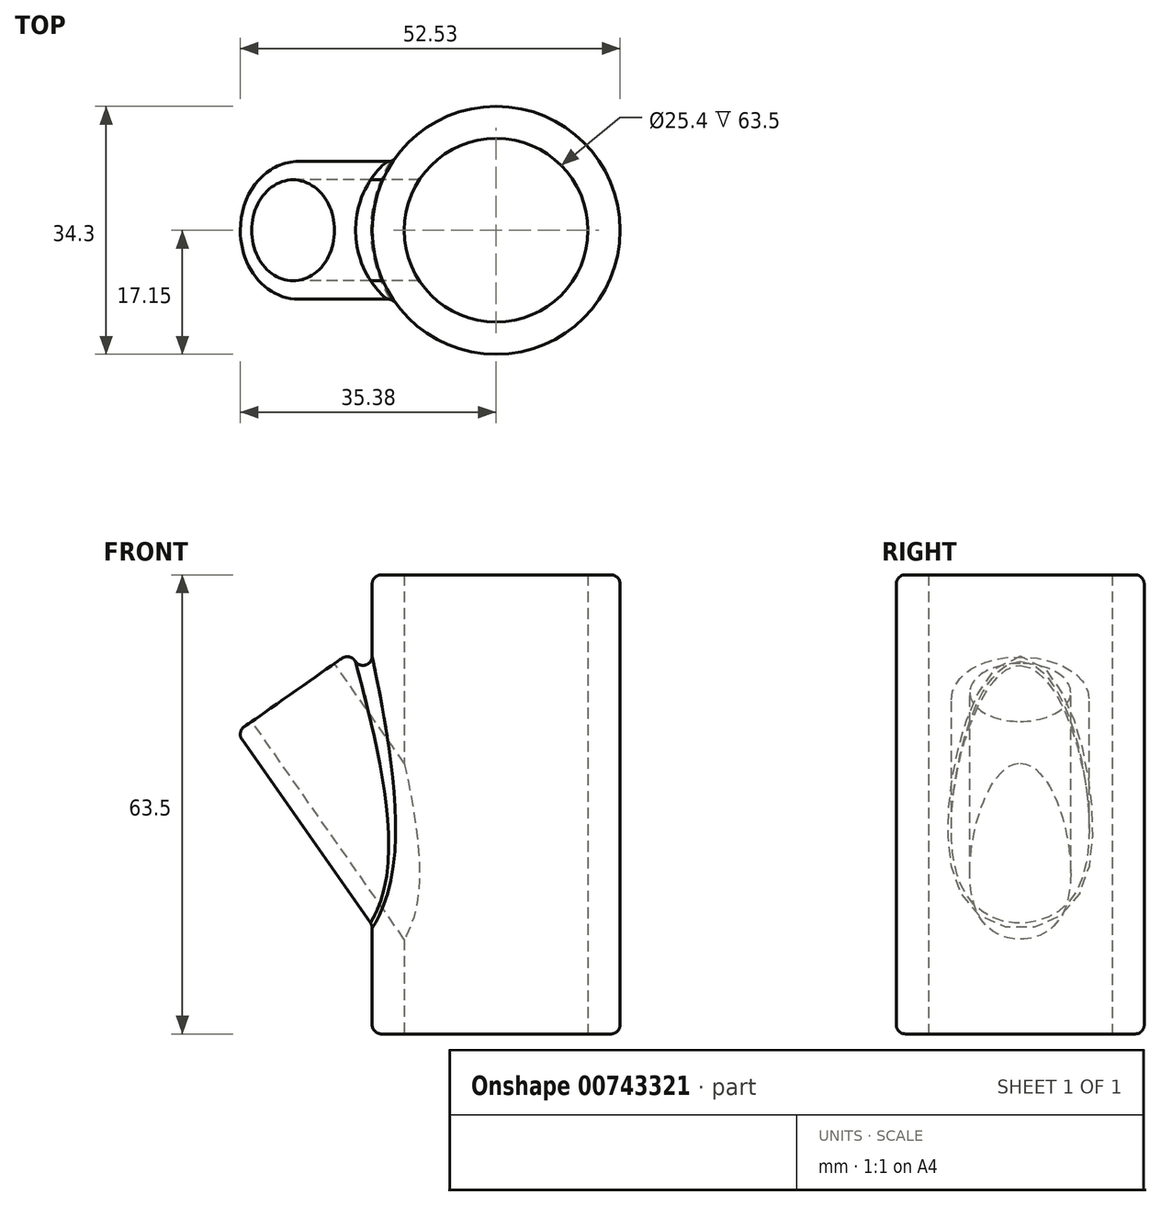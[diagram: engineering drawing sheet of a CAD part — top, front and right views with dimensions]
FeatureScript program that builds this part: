
annotation { "Feature Type Name" : "Feature", "Feature Type Description" : "" }
export const myFeature = defineFeature(function(context is Context, id is Id, definition is map)
    precondition{}
    {
        {
            var Q0;
            Q0=qCreatedBy(makeId("Top.planeOp"),FACE);
            var sketch = newSketch(context, id + "F0", { "sketchPlane" : qUnion([Q0])});
            skCircle(sketch, "E0", {"center": v(0, 0) * mm, "radius": 12.7 * mm});
            skCircle(sketch, "E1", {"center": v(0, 0) * mm, "radius": 17.15 * mm});
            skSolve(sketch);
        }
        {
            var Q0;
            Q0=makeQuery(id+"F0.imprint","IMPRINT",FACE,{"disambiguationData":[TD([[makeQuery(id+"F0.imprint","IMPRINT",EDGE,{"derivedFrom":sQuery(id+"F0.wireOp",EDGE,"E0")}),-1.0]])]});
            extrude(context, id + "F1", {"entities" : qUnion([Q0]), "depth" : 63.5 * mm, "offsetDistance" : 25.4 * mm});
        }
        {
            var Q0;
            Q0=qCreatedBy(makeId("Right.planeOp"),FACE);
            cPlane(context, id + "F2", {"entities" : qUnion([Q0]), "cplaneType" : CPlaneType.OFFSET, "offset" : 16.76 * mm, "oppositeDirection" : true, "width" : 152.4 * mm, "height" : 152.4 * mm});
        }
        {
            var Q0;
            Q0=qCreatedBy(id+"F2.planeOp",FACE);
            var sketch = newSketch(context, id + "F3", { "sketchPlane" : qUnion([Q0])});
            skLineSegment(sketch, "E2", {"start": v(45.22, 55.14) * mm, "end": v(-44.35, 55.14) * mm});
            skSolve(sketch);
        }
        {
            var Q0;
            Q0=sQuery(id+"F3.wireOp",EDGE,"E2");
            cPlane(context, id + "F4", {"entities" : qUnion([Q0]), "cplaneType" : CPlaneType.LINE_ANGLE, "offset" : 25.4 * mm, "angle" : 35 * degree, "width" : 152.4 * mm, "height" : 152.4 * mm});
        }
        {
            var Q0;
            Q0=qCreatedBy(id+"F4.planeOp",FACE);
            var sketch = newSketch(context, id + "F5", { "sketchPlane" : qUnion([Q0])});
            skCircle(sketch, "E3", {"center": v(4.09, 0) * mm, "radius": 6.99 * mm});
            skCircle(sketch, "E4", {"center": v(4.09, 0) * mm, "radius": 9.53 * mm});
            skSolve(sketch);
        }
        {
            var Q0;
            Q0=makeQuery(id+"F5.imprint","IMPRINT",FACE,{"disambiguationData":[TD([[makeQuery(id+"F5.imprint","IMPRINT",EDGE,{"derivedFrom":sQuery(id+"F5.wireOp",EDGE,"E3")}),-1.0]])]});
            extrude(context, id + "F6", {"entities" : qUnion([Q0]), "operationType" : NewBodyOperationType.ADD, "depth" : 35.56 * mm, "offsetDistance" : 25.4 * mm});
        }
        {
            var Q0;
            Q0=makeQuery(id+"F6.opExtrude","CAP_FACE",FACE,{"disambiguationData":[OSD([sQuery(id+"F5.wireOp",EDGE,"E3"),sQuery(id+"F5.wireOp",EDGE,"E4")])],"isStart":true});
            var sketch = newSketch(context, id + "F7", { "sketchPlane" : qUnion([Q0])});
            skCircle(sketch, "E5", {"center": v(4.09, 0) * mm, "radius": 6.99 * mm});
            skSolve(sketch);
        }
        {
            var Q0;
            Q0 = qSketchRegion(id + "F7", true);
            extrude(context, id + "F8", {"entities" : qUnion([Q0]), "operationType" : NewBodyOperationType.REMOVE, "oppositeDirection" : true, "depth" : 43.38 * mm, "offsetDistance" : 25.4 * mm});
        }
        {
            var Q0;
            {var subQ0=sQuery(id+"F5.wireOp",EDGE,"E4");Q0=makeQuery(id+"F6.boolean.opBoolean","SPLIT",FACE,{"disambiguationData":[TD([makeQuery(id+"F1.opExtrude","SWEPT_FACE",FACE,{"disambiguationData":[OSD([sQuery(id+"F0.wireOp",EDGE,"E1")])]})])],"derivedFrom":makeQuery(id+"F6.opExtrude","SWEPT_FACE",FACE,{"disambiguationData":[OSD([subQ0])]})});}
            var Q1;
            Q1=makeQuery(id+"F1.opExtrude","CAP_EDGE",EDGE,{"disambiguationData":[OSD([sQuery(id+"F0.wireOp",EDGE,"E1")])],"isStart":false});
            var Q2;
            Q2=makeQuery(id+"F1.opExtrude","CAP_EDGE",EDGE,{"disambiguationData":[OSD([sQuery(id+"F0.wireOp",EDGE,"E1")])],"isStart":true});
            fillet(context, id + "F9", {"entities" : qUnion([Q0, Q1, Q2]), "radius" : 1.27 * mm, "tangentPropagation" : true, "allowEdgeOverflow" : false});
        }
        {
            var Q0;
            Q0=makeQuery(id+"F1.opExtrude","CAP_FACE",FACE,{"disambiguationData":[OSD([sQuery(id+"F0.wireOp",EDGE,"E0"),sQuery(id+"F0.wireOp",EDGE,"E1")])],"isStart":true});
            var sketch = newSketch(context, id + "F10", { "sketchPlane" : qUnion([Q0])});
            skCircle(sketch, "E6", {"center": v(0, 0) * mm, "radius": 12.7 * mm});
            skSolve(sketch);
        }
        {
            var Q0;
            Q0 = qSketchRegion(id + "F10", true);
            extrude(context, id + "F11", {"entities" : qUnion([Q0]), "operationType" : NewBodyOperationType.REMOVE, "oppositeDirection" : true, "depth" : 68.07 * mm, "offsetDistance" : 25.4 * mm});
        }
    });
